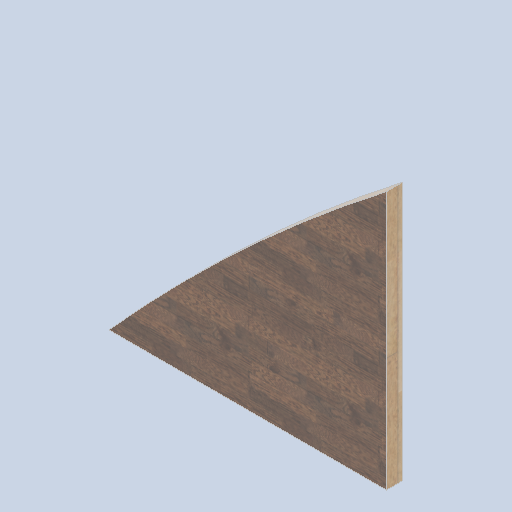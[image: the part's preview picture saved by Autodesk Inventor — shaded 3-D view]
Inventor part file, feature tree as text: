
AUTODESK INVENTOR PART (.ipt)
format: ipt  version: 2024.2 (Build 282272000, 272)  size: 172,544 bytes
history: native  units: in
note: dims shown in document units (in); Inventor stores cm internally (conversion verified against a paired STEP export)
features: other x3, sketch x1
ambient origin geometry x8: Origin, YZ Plane, XZ Plane, XY Plane, X Axis, Y Axis, Z Axis, Center Point
bodies: Solid1 (feature_tree)
feature tree (4):
  other  "front_wall_block01.ipt"
  other  "Solid1::front_wall_block01.ipt"
  other  "TaggingFeature1"
  sketch  "Sketch1"  dims[d0=0.3937in]
